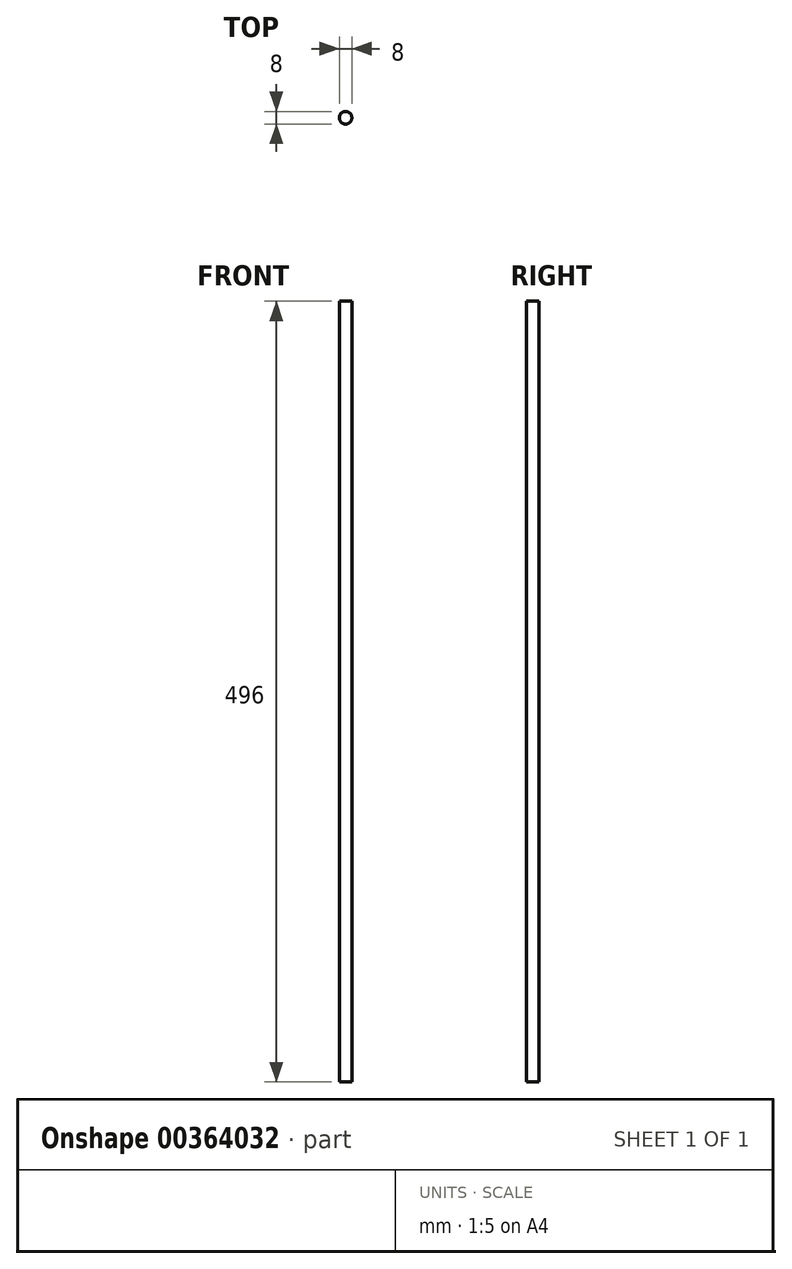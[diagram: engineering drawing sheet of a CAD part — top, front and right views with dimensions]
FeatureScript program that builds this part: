
annotation { "Feature Type Name" : "Feature", "Feature Type Description" : "" }
export const myFeature = defineFeature(function(context is Context, id is Id, definition is map)
    precondition{}
    {
        {
            var Q0;
            Q0=qCreatedBy(makeId("Top.planeOp"),FACE);
            var sketch = newSketch(context, id + "F0", { "sketchPlane" : qUnion([Q0])});
            skCircle(sketch, "E0", {"center": v(0, 0) * mm, "radius": 4 * mm});
            skSolve(sketch);
        }
        {
            var Q0;
            Q0 = qSketchRegion(id + "F0", true);
            var Q1;
            Q1=sQuery(id+"F0.wireOp",EDGE,"E0");
            extrude(context, id + "F1", {"entities" : qUnion([Q0]), "surfaceEntities" : qUnion([Q1]), "depth" : 496 * mm});
        }
    });
